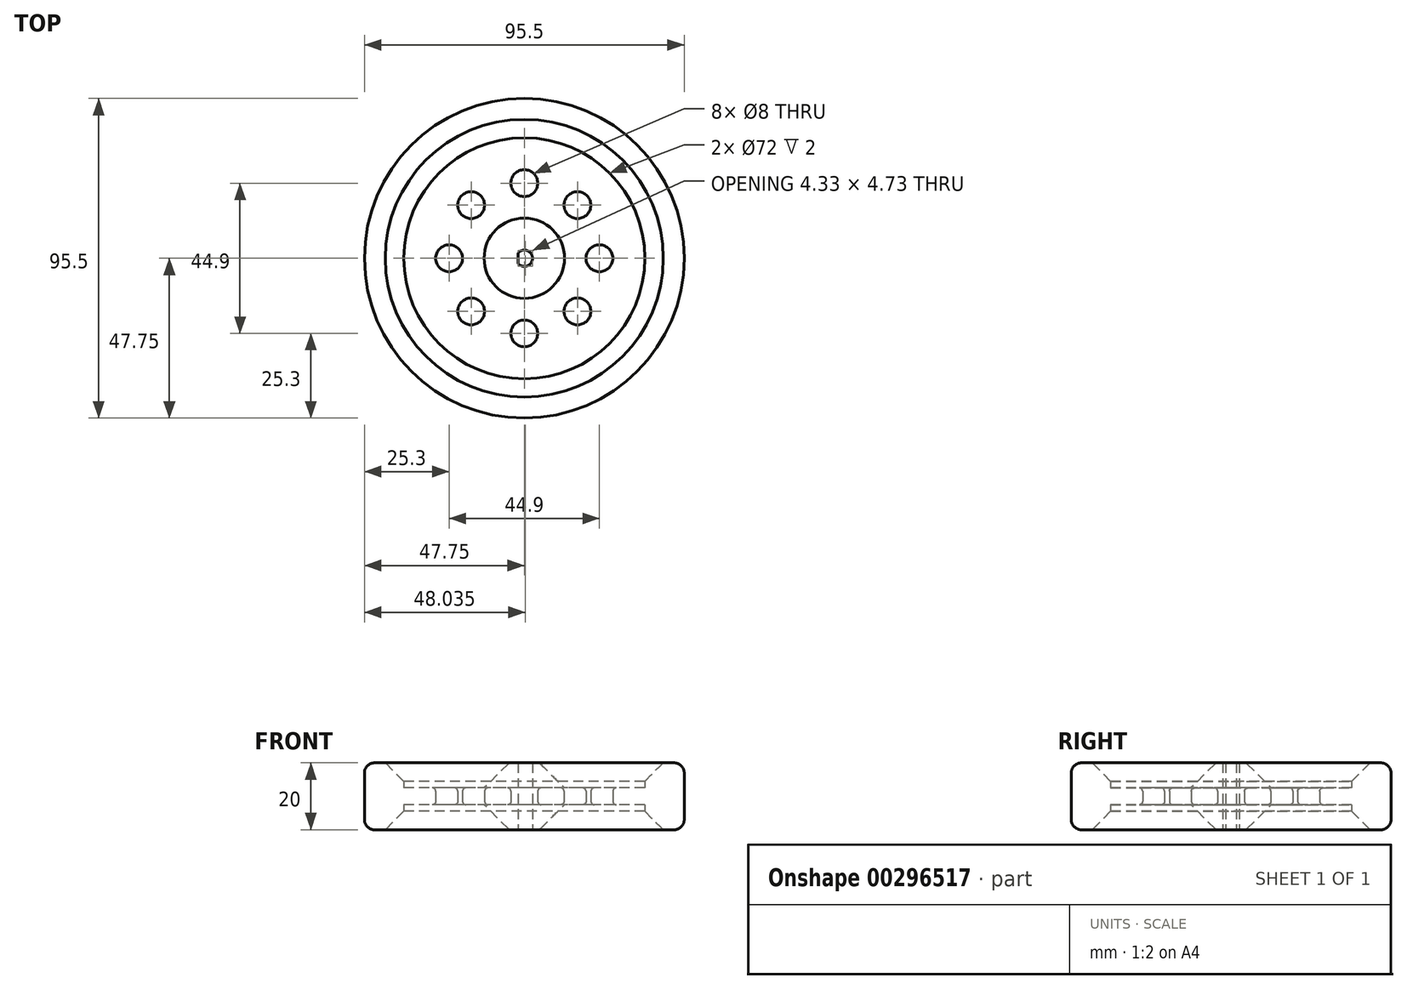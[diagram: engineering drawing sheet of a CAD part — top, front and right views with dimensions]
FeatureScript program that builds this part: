
annotation { "Feature Type Name" : "Feature", "Feature Type Description" : "" }
export const myFeature = defineFeature(function(context is Context, id is Id, definition is map)
    precondition{}
    {
        {
            var Q0;
            Q0=qCreatedBy(makeId("Top.planeOp"),FACE);
            var sketch = newSketch(context, id + "F0", { "sketchPlane" : qUnion([Q0])});
            skCircle(sketch, "E0", {"center": v(0, 0) * mm, "radius": 47.75 * mm});
            skCircle(sketch, "E1", {"center": v(0, 0) * mm, "radius": 44 * mm});
            skArc(sketch, "E2", {"start": v(-1.88, -1.57) * mm, "mid": v(2.45, 0) * mm, "end": v(-1.88, 1.57) * mm});
            skLineSegment(sketch, "E3", {"start": v(-1.88, -1.57) * mm, "end": v(-1.88, 1.57) * mm});
            skCircle(sketch, "E4", {"center": v(0, 0) * mm, "radius": 42.5 * mm});
            skCircle(sketch, "E5", {"center": v(0, 0) * mm, "radius": 36 * mm});
            skSolve(sketch);
        }
        {
            var Q0;
            Q0=makeQuery(id+"F0.imprint","IMPRINT",FACE,{"disambiguationData":[TD([[makeQuery(id+"F0.imprint","IMPRINT",EDGE,{"derivedFrom":sQuery(id+"F0.wireOp",EDGE,"E2")}),-1.0]])]});
            var Q1;
            Q1=makeQuery(id+"F0.imprint","IMPRINT",FACE,{"disambiguationData":[TD([[makeQuery(id+"F0.imprint","IMPRINT",EDGE,{"derivedFrom":sQuery(id+"F0.wireOp",EDGE,"8wvdLqEF-Mvgu-ieMB-92kP-JiN9EquYggHF")}),1.0]])]});
            extrude(context, id + "F1", {"entities" : qUnion([Q0, Q1]), "depth" : 12.5 * mm, "hasSecondDirection" : true, "secondDirectionOppositeDirection" : false, "secondDirectionDepth" : 7.5 * mm});
        }
        {
            var Q0;
            Q0=makeQuery(id+"F0.imprint","IMPRINT",FACE,{"disambiguationData":[TD([[makeQuery(id+"F0.imprint","IMPRINT",EDGE,{"derivedFrom":sQuery(id+"F0.wireOp",EDGE,"E4")}),1.0]])]});
            var Q1;
            Q1=makeQuery(id+"F0.imprint","IMPRINT",FACE,{"disambiguationData":[TD([[makeQuery(id+"F0.imprint","IMPRINT",EDGE,{"derivedFrom":sQuery(id+"F0.wireOp",EDGE,"E1")}),1.0]])]});
            extrude(context, id + "F2", {"entities" : qUnion([Q0, Q1]), "operationType" : NewBodyOperationType.ADD, "depth" : 20 * mm});
        }
        {
            var Q0;
            Q0=makeQuery(id+"F0.imprint","IMPRINT",FACE,{"disambiguationData":[TD([[makeQuery(id+"F0.imprint","IMPRINT",EDGE,{"derivedFrom":sQuery(id+"F0.wireOp",EDGE,"E0")}),1.0]])]});
            extrude(context, id + "F3", {"entities" : qUnion([Q0]), "depth" : 20 * mm});
        }
        {
            var Q0;
            Q0=makeQuery(id+"F0.imprint","IMPRINT",FACE,{"disambiguationData":[TD([[makeQuery(id+"F0.imprint","IMPRINT",EDGE,{"derivedFrom":sQuery(id+"F0.wireOp",EDGE,"E1")}),1.0]])]});
            extrude(context, id + "F4", {"entities" : qUnion([Q0]), "operationType" : NewBodyOperationType.REMOVE, "depth" : 1 * mm});
        }
        {
            var Q0;
            Q0=makeQuery(id+"F0.imprint","IMPRINT",FACE,{"disambiguationData":[TD([[makeQuery(id+"F0.imprint","IMPRINT",EDGE,{"derivedFrom":sQuery(id+"F0.wireOp",EDGE,"E1")}),1.0]])]});
            extrude(context, id + "F5", {"entities" : qUnion([Q0]), "operationType" : NewBodyOperationType.ADD, "depth" : 1 * mm});
        }
        {
            var Q0;
            Q0=makeQuery(id+"F0.imprint","IMPRINT",FACE,{"disambiguationData":[TD([[makeQuery(id+"F0.imprint","IMPRINT",EDGE,{"derivedFrom":sQuery(id+"F0.wireOp",EDGE,"E1")}),1.0]])]});
            extrude(context, id + "F6", {"entities" : qUnion([Q0]), "operationType" : NewBodyOperationType.REMOVE, "depth" : 20 * mm, "hasSecondDirection" : true, "secondDirectionOppositeDirection" : false, "secondDirectionDepth" : 19 * mm});
        }
        {
            var Q0;
            Q0=makeQuery(id+"F0.imprint","IMPRINT",FACE,{"disambiguationData":[TD([[makeQuery(id+"F0.imprint","IMPRINT",EDGE,{"derivedFrom":sQuery(id+"F0.wireOp",EDGE,"E1")}),1.0]])]});
            extrude(context, id + "F7", {"entities" : qUnion([Q0]), "operationType" : NewBodyOperationType.ADD, "depth" : 20 * mm, "hasSecondDirection" : true, "secondDirectionOppositeDirection" : false, "secondDirectionDepth" : 19 * mm});
        }
        {
            var Q0;
            Q0=makeQuery(id+"F1.opExtrude","CAP_FACE",FACE,{"disambiguationData":[OSD([sQuery(id+"F0.wireOp",EDGE,"E2"),sQuery(id+"F0.wireOp",EDGE,"E3"),sQuery(id+"F0.wireOp",EDGE,"E5")])],"isStart":false});
            var sketch = newSketch(context, id + "F8", { "sketchPlane" : qUnion([Q0])});
            skCircle(sketch, "E6", {"center": v(0, 0) * mm, "radius": 12.5 * mm});
            skSolve(sketch);
        }
        {
            var Q0;
            Q0=makeQuery(id+"F8.imprint","IMPRINT",FACE,{"disambiguationData":[TD([[makeQuery(id+"F8.imprint","IMPRINT",EDGE,{"derivedFrom":sQuery(id+"F8.wireOp",EDGE,"E6")}),1.0]])]});
            extrude(context, id + "F9", {"entities" : qUnion([Q0]), "operationType" : NewBodyOperationType.ADD, "depth" : 7.5 * mm, "hasSecondDirection" : true, "secondDirectionOppositeDirection" : true, "secondDirectionDepth" : 12.5 * mm});
        }
        {
            var Q0;
            Q0=makeQuery(id+"F9.opExtrude","CAP_EDGE",EDGE,{"disambiguationData":[OSD([sQuery(id+"F8.wireOp",EDGE,"E6")])],"isStart":false});
            var Q1;
            Q1=makeQuery(id+"F9.opExtrude","CAP_EDGE",EDGE,{"disambiguationData":[OSD([sQuery(id+"F8.wireOp",EDGE,"E6")])],"isStart":true});
            chamfer(context, id + "F10", {"entities" : qUnion([Q0, Q1]), "width" : 8 * mm, "tangentPropagation" : true});
        }
        {
            var Q0;
            {var subQ0=sQuery(id+"F0.wireOp",EDGE,"E2");Q0=makeQuery(id+"F8.imprint","IMPRINT",FACE,{"disambiguationData":[TD([[makeQuery(id+"F8.imprint","IMPRINT",EDGE,{"derivedFrom":makeQuery(id+"F1.opExtrude","CAP_EDGE",EDGE,{"disambiguationData":[OSD([subQ0])],"isStart":false})}),-1.0]])]});}
            var sketch = newSketch(context, id + "F11", { "sketchPlane" : qUnion([Q0])});
            skCircle(sketch, "E7", {"center": v(0, 22.45) * mm, "radius": 4 * mm});
            skCircle(sketch, "E8", {"center": v(0, 0) * mm, "radius": 5 * mm});
            skSolve(sketch);
        }
        {
            var Q0;
            Q0=makeQuery(id+"F11.imprint","IMPRINT",FACE,{"disambiguationData":[TD([[makeQuery(id+"F11.imprint","IMPRINT",EDGE,{"derivedFrom":sQuery(id+"F11.wireOp",EDGE,"E7")}),1.0]])]});
            extrude(context, id + "F12", {"entities" : qUnion([Q0]), "depth" : 25 * mm, "hasSecondDirection" : true, "secondDirectionOppositeDirection" : true, "secondDirectionDepth" : 25 * mm});
        }
        {
            var Q0;
            Q0=makeQuery(id+"F12.opExtrude","SWEPT_BODY",BODY,{"disambiguationData":[OSD([sQuery(id+"F11.wireOp",EDGE,"E7")])]});
            var Q1;
            Q1=sQuery(id+"F11.wireOp",EDGE,"E8");
            circularPattern(context, id + "F13", {"operationType" : NewBodyOperationType.REMOVE, "entities" : qUnion([Q0]), "axis" : qUnion([Q1]), "angle" : 360 * degree, "instanceCount" : 8, "equalSpace" : true});
        }
        {
            var Q0;
            Q0=makeQuery(id+"F2.opExtrude","CAP_EDGE",EDGE,{"disambiguationData":[OSD([sQuery(id+"F0.wireOp",EDGE,"E5")])],"isStart":false});
            var Q1;
            Q1=makeQuery(id+"F2.opExtrude","CAP_EDGE",EDGE,{"disambiguationData":[OSD([sQuery(id+"F0.wireOp",EDGE,"E5")])],"isStart":true});
            chamfer(context, id + "F14", {"entities" : qUnion([Q0, Q1]), "width" : 5.5 * mm, "tangentPropagation" : true});
        }
        {
            var Q0;
            Q0=makeQuery(id+"F13.boolean.opBoolean","INTERSECT",EDGE,{"derivedFrom":[makeQuery(id+"F1.opExtrude","CAP_FACE",FACE,{"disambiguationData":[OSD([sQuery(id+"F0.wireOp",EDGE,"E2"),sQuery(id+"F0.wireOp",EDGE,"E3"),sQuery(id+"F0.wireOp",EDGE,"E5")])],"isStart":false}),makeQuery(id+"F13.opPattern","COPY",FACE,{"derivedFrom":makeQuery(id+"F12.opExtrude","SWEPT_FACE",FACE,{"disambiguationData":[OSD([sQuery(id+"F11.wireOp",EDGE,"E7")])]}),"instanceName":"3"})]});
            var Q1;
            Q1=makeQuery(id+"F13.boolean.opBoolean","INTERSECT",EDGE,{"derivedFrom":[makeQuery(id+"F1.opExtrude","CAP_FACE",FACE,{"disambiguationData":[OSD([sQuery(id+"F0.wireOp",EDGE,"E2"),sQuery(id+"F0.wireOp",EDGE,"E3"),sQuery(id+"F0.wireOp",EDGE,"E5")])],"isStart":false}),makeQuery(id+"F13.opPattern","COPY",FACE,{"derivedFrom":makeQuery(id+"F12.opExtrude","SWEPT_FACE",FACE,{"disambiguationData":[OSD([sQuery(id+"F11.wireOp",EDGE,"E7")])]}),"instanceName":"4"})]});
            var Q2;
            Q2=makeQuery(id+"F13.boolean.opBoolean","INTERSECT",EDGE,{"derivedFrom":[makeQuery(id+"F1.opExtrude","CAP_FACE",FACE,{"disambiguationData":[OSD([sQuery(id+"F0.wireOp",EDGE,"E2"),sQuery(id+"F0.wireOp",EDGE,"E3"),sQuery(id+"F0.wireOp",EDGE,"E5")])],"isStart":false}),makeQuery(id+"F13.opPattern","COPY",FACE,{"derivedFrom":makeQuery(id+"F12.opExtrude","SWEPT_FACE",FACE,{"disambiguationData":[OSD([sQuery(id+"F11.wireOp",EDGE,"E7")])]}),"instanceName":"2"})]});
            var Q3;
            Q3=makeQuery(id+"F13.boolean.opBoolean","INTERSECT",EDGE,{"derivedFrom":[makeQuery(id+"F1.opExtrude","CAP_FACE",FACE,{"disambiguationData":[OSD([sQuery(id+"F0.wireOp",EDGE,"E2"),sQuery(id+"F0.wireOp",EDGE,"E3"),sQuery(id+"F0.wireOp",EDGE,"E5")])],"isStart":false}),makeQuery(id+"F13.opPattern","COPY",FACE,{"derivedFrom":makeQuery(id+"F12.opExtrude","SWEPT_FACE",FACE,{"disambiguationData":[OSD([sQuery(id+"F11.wireOp",EDGE,"E7")])]}),"instanceName":"1"})]});
            var Q4;
            Q4=makeQuery(id+"F13.boolean.opBoolean","INTERSECT",EDGE,{"derivedFrom":[makeQuery(id+"F1.opExtrude","CAP_FACE",FACE,{"disambiguationData":[OSD([sQuery(id+"F0.wireOp",EDGE,"E2"),sQuery(id+"F0.wireOp",EDGE,"E3"),sQuery(id+"F0.wireOp",EDGE,"E5")])],"isStart":false}),makeQuery(id+"F12.opExtrude","SWEPT_FACE",FACE,{"disambiguationData":[OSD([sQuery(id+"F11.wireOp",EDGE,"E7")])]})]});
            var Q5;
            Q5=makeQuery(id+"F13.boolean.opBoolean","INTERSECT",EDGE,{"derivedFrom":[makeQuery(id+"F1.opExtrude","CAP_FACE",FACE,{"disambiguationData":[OSD([sQuery(id+"F0.wireOp",EDGE,"E2"),sQuery(id+"F0.wireOp",EDGE,"E3"),sQuery(id+"F0.wireOp",EDGE,"E5")])],"isStart":false}),makeQuery(id+"F13.opPattern","COPY",FACE,{"derivedFrom":makeQuery(id+"F12.opExtrude","SWEPT_FACE",FACE,{"disambiguationData":[OSD([sQuery(id+"F11.wireOp",EDGE,"E7")])]}),"instanceName":"7"})]});
            var Q6;
            Q6=makeQuery(id+"F13.boolean.opBoolean","INTERSECT",EDGE,{"derivedFrom":[makeQuery(id+"F1.opExtrude","CAP_FACE",FACE,{"disambiguationData":[OSD([sQuery(id+"F0.wireOp",EDGE,"E2"),sQuery(id+"F0.wireOp",EDGE,"E3"),sQuery(id+"F0.wireOp",EDGE,"E5")])],"isStart":false}),makeQuery(id+"F13.opPattern","COPY",FACE,{"derivedFrom":makeQuery(id+"F12.opExtrude","SWEPT_FACE",FACE,{"disambiguationData":[OSD([sQuery(id+"F11.wireOp",EDGE,"E7")])]}),"instanceName":"6"})]});
            var Q7;
            Q7=makeQuery(id+"F13.boolean.opBoolean","INTERSECT",EDGE,{"derivedFrom":[makeQuery(id+"F1.opExtrude","CAP_FACE",FACE,{"disambiguationData":[OSD([sQuery(id+"F0.wireOp",EDGE,"E2"),sQuery(id+"F0.wireOp",EDGE,"E3"),sQuery(id+"F0.wireOp",EDGE,"E5")])],"isStart":false}),makeQuery(id+"F13.opPattern","COPY",FACE,{"derivedFrom":makeQuery(id+"F12.opExtrude","SWEPT_FACE",FACE,{"disambiguationData":[OSD([sQuery(id+"F11.wireOp",EDGE,"E7")])]}),"instanceName":"5"})]});
            var Q8;
            {var subQ0=sQuery(id+"F8.wireOp",EDGE,"E6");Q8=makeQuery(id+"F10.opChamfer","BLEND_EDGE",EDGE,{"blendedFrom":[makeQuery(id+"F9.opExtrude","CAP_EDGE",EDGE,{"disambiguationData":[OSD([subQ0])],"isStart":false}),makeQuery(id+"F9.opExtrude","CAP_FACE",FACE,{"disambiguationData":[OSD([sQuery(id+"F0.wireOp",EDGE,"E2"),sQuery(id+"F0.wireOp",EDGE,"E3"),subQ0])],"isStart":false})],"blendedInto":[makeQuery(id+"F9.opExtrude","CAP_FACE",FACE,{"disambiguationData":[OSD([sQuery(id+"F0.wireOp",EDGE,"E2"),sQuery(id+"F0.wireOp",EDGE,"E3"),subQ0])],"isStart":false})]});}
            var Q9;
            Q9=makeQuery(id+"F13.boolean.opBoolean","INTERSECT",EDGE,{"derivedFrom":[makeQuery(id+"F1.opExtrude","CAP_FACE",FACE,{"disambiguationData":[OSD([sQuery(id+"F0.wireOp",EDGE,"E2"),sQuery(id+"F0.wireOp",EDGE,"E3"),sQuery(id+"F0.wireOp",EDGE,"E5")])],"isStart":true}),makeQuery(id+"F13.opPattern","COPY",FACE,{"derivedFrom":makeQuery(id+"F12.opExtrude","SWEPT_FACE",FACE,{"disambiguationData":[OSD([sQuery(id+"F11.wireOp",EDGE,"E7")])]}),"instanceName":"6"})]});
            var Q10;
            Q10=makeQuery(id+"F13.boolean.opBoolean","INTERSECT",EDGE,{"derivedFrom":[makeQuery(id+"F1.opExtrude","CAP_FACE",FACE,{"disambiguationData":[OSD([sQuery(id+"F0.wireOp",EDGE,"E2"),sQuery(id+"F0.wireOp",EDGE,"E3"),sQuery(id+"F0.wireOp",EDGE,"E5")])],"isStart":true}),makeQuery(id+"F13.opPattern","COPY",FACE,{"derivedFrom":makeQuery(id+"F12.opExtrude","SWEPT_FACE",FACE,{"disambiguationData":[OSD([sQuery(id+"F11.wireOp",EDGE,"E7")])]}),"instanceName":"5"})]});
            var Q11;
            Q11=makeQuery(id+"F13.boolean.opBoolean","INTERSECT",EDGE,{"derivedFrom":[makeQuery(id+"F1.opExtrude","CAP_FACE",FACE,{"disambiguationData":[OSD([sQuery(id+"F0.wireOp",EDGE,"E2"),sQuery(id+"F0.wireOp",EDGE,"E3"),sQuery(id+"F0.wireOp",EDGE,"E5")])],"isStart":true}),makeQuery(id+"F13.opPattern","COPY",FACE,{"derivedFrom":makeQuery(id+"F12.opExtrude","SWEPT_FACE",FACE,{"disambiguationData":[OSD([sQuery(id+"F11.wireOp",EDGE,"E7")])]}),"instanceName":"4"})]});
            var Q12;
            Q12=makeQuery(id+"F13.boolean.opBoolean","INTERSECT",EDGE,{"derivedFrom":[makeQuery(id+"F1.opExtrude","CAP_FACE",FACE,{"disambiguationData":[OSD([sQuery(id+"F0.wireOp",EDGE,"E2"),sQuery(id+"F0.wireOp",EDGE,"E3"),sQuery(id+"F0.wireOp",EDGE,"E5")])],"isStart":true}),makeQuery(id+"F13.opPattern","COPY",FACE,{"derivedFrom":makeQuery(id+"F12.opExtrude","SWEPT_FACE",FACE,{"disambiguationData":[OSD([sQuery(id+"F11.wireOp",EDGE,"E7")])]}),"instanceName":"3"})]});
            var Q13;
            Q13=makeQuery(id+"F13.boolean.opBoolean","INTERSECT",EDGE,{"derivedFrom":[makeQuery(id+"F1.opExtrude","CAP_FACE",FACE,{"disambiguationData":[OSD([sQuery(id+"F0.wireOp",EDGE,"E2"),sQuery(id+"F0.wireOp",EDGE,"E3"),sQuery(id+"F0.wireOp",EDGE,"E5")])],"isStart":true}),makeQuery(id+"F13.opPattern","COPY",FACE,{"derivedFrom":makeQuery(id+"F12.opExtrude","SWEPT_FACE",FACE,{"disambiguationData":[OSD([sQuery(id+"F11.wireOp",EDGE,"E7")])]}),"instanceName":"2"})]});
            var Q14;
            Q14=makeQuery(id+"F13.boolean.opBoolean","INTERSECT",EDGE,{"derivedFrom":[makeQuery(id+"F1.opExtrude","CAP_FACE",FACE,{"disambiguationData":[OSD([sQuery(id+"F0.wireOp",EDGE,"E2"),sQuery(id+"F0.wireOp",EDGE,"E3"),sQuery(id+"F0.wireOp",EDGE,"E5")])],"isStart":true}),makeQuery(id+"F13.opPattern","COPY",FACE,{"derivedFrom":makeQuery(id+"F12.opExtrude","SWEPT_FACE",FACE,{"disambiguationData":[OSD([sQuery(id+"F11.wireOp",EDGE,"E7")])]}),"instanceName":"1"})]});
            var Q15;
            Q15=makeQuery(id+"F13.boolean.opBoolean","INTERSECT",EDGE,{"derivedFrom":[makeQuery(id+"F1.opExtrude","CAP_FACE",FACE,{"disambiguationData":[OSD([sQuery(id+"F0.wireOp",EDGE,"E2"),sQuery(id+"F0.wireOp",EDGE,"E3"),sQuery(id+"F0.wireOp",EDGE,"E5")])],"isStart":true}),makeQuery(id+"F12.opExtrude","SWEPT_FACE",FACE,{"disambiguationData":[OSD([sQuery(id+"F11.wireOp",EDGE,"E7")])]})]});
            var Q16;
            {var subQ0=sQuery(id+"F8.wireOp",EDGE,"E6");Q16=makeQuery(id+"F10.opChamfer","BLEND_EDGE",EDGE,{"blendedFrom":[makeQuery(id+"F9.opExtrude","CAP_EDGE",EDGE,{"disambiguationData":[OSD([subQ0])],"isStart":true}),makeQuery(id+"F9.opExtrude","CAP_FACE",FACE,{"disambiguationData":[OSD([sQuery(id+"F0.wireOp",EDGE,"E2"),sQuery(id+"F0.wireOp",EDGE,"E3"),subQ0])],"isStart":true})],"blendedInto":[makeQuery(id+"F9.opExtrude","CAP_FACE",FACE,{"disambiguationData":[OSD([sQuery(id+"F0.wireOp",EDGE,"E2"),sQuery(id+"F0.wireOp",EDGE,"E3"),subQ0])],"isStart":true})]});}
            var Q17;
            Q17=makeQuery(id+"F13.boolean.opBoolean","INTERSECT",EDGE,{"derivedFrom":[makeQuery(id+"F1.opExtrude","CAP_FACE",FACE,{"disambiguationData":[OSD([sQuery(id+"F0.wireOp",EDGE,"E2"),sQuery(id+"F0.wireOp",EDGE,"E3"),sQuery(id+"F0.wireOp",EDGE,"E5")])],"isStart":true}),makeQuery(id+"F13.opPattern","COPY",FACE,{"derivedFrom":makeQuery(id+"F12.opExtrude","SWEPT_FACE",FACE,{"disambiguationData":[OSD([sQuery(id+"F11.wireOp",EDGE,"E7")])]}),"instanceName":"7"})]});
            fillet(context, id + "F15", {"entities" : qUnion([Q0, Q1, Q2, Q3, Q4, Q5, Q6, Q7, Q8, Q9, Q10, Q11, Q12, Q13, Q14, Q15, Q16, Q17]), "radius" : 1 * mm, "tangentPropagation" : true, "allowEdgeOverflow" : false});
        }
        {
            var Q0;
            Q0=makeQuery(id+"F3.opExtrude","CAP_EDGE",EDGE,{"disambiguationData":[OSD([sQuery(id+"F0.wireOp",EDGE,"E0")])],"isStart":false});
            var Q1;
            Q1=makeQuery(id+"F3.opExtrude","CAP_EDGE",EDGE,{"disambiguationData":[OSD([sQuery(id+"F0.wireOp",EDGE,"E0")])],"isStart":true});
            fillet(context, id + "F16", {"entities" : qUnion([Q0, Q1]), "radius" : 3 * mm, "tangentPropagation" : true, "allowEdgeOverflow" : false});
        }
    });
